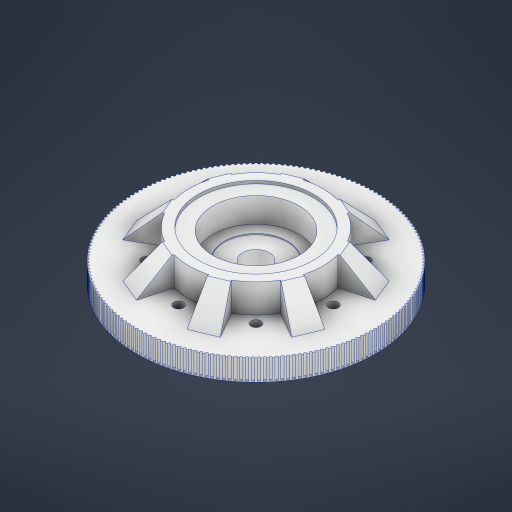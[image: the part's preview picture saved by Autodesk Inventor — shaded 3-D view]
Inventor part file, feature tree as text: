
AUTODESK INVENTOR PART (.ipt)
format: ipt  version: 2024 (Build 280153000, 153)  size: 658,944 bytes
history: native  units: mm
features: extrude x8, sketch x8, pattern_circular x2, chamfer x1, projected_geometry x1
ambient origin geometry x8: Origin, YZ Plane, XZ Plane, XY Plane, X Axis, Y Axis, Z Axis, Center Point
bodies: Solid1 (feature_tree)
feature tree (20):
  extrude  "Extrusion1"  Depth=22.0mm TaperAngle=0.0deg
  extrude  "Extrusion2"  Depth=21.0mm TaperAngle=0.0deg
  extrude  "Extrusion3"  Depth=90.0mm
  pattern_circular  "Circular Pattern1"  Count=14  [1 undecoded]
  extrude  "Extrusion4"  Depth=3.0mm TaperAngle=0.0deg
  extrude  "Extrusion5"  Depth=80.0mm TaperAngle=360.0deg
  extrude  "Extrusion6"  TaperAngle=15.0deg  [1 undecoded]
  extrude  "Extrusion7"  Depth=1.308997mm
  extrude  "Extrusion8"  Depth=30.0mm TaperAngle=0.0deg
  chamfer  "Chamfer1"  Distance=30.0mm Angle=45.0deg
  pattern_circular  "Circular Pattern2"  Count=8 Angle=360.0deg
  sketch  "Sketch1"  dims[d0=250.0mm d1=22.0mm d2=0.0mm]
  sketch  "Sketch2"  dims[d3=30.0mm d4=0.0mm d5=21.0mm d6=0.0mm]
  projected_geometry  "Projected Loop1"
  sketch  "Sketch3"  dims[d7=1800.0mm d8=360.0deg d10=90.0mm d11=140.0mm]
  sketch  "Sketch4"  dims[d12=1.0mm d13=0.0mm d14=3.0mm d15=0.0mm]
  sketch  "Sketch5"  dims[d16=25.0mm d17=0.0mm d18=80.0mm d20=360.0deg]
  sketch  "Sketch6"  dims[d22=20.0mm d23=0.0mm d24=15.0deg]
  sketch  "Sketch7"  dims[d25=60.0deg d26=1.308997mm]
  sketch  "Sketch8"  dims[d27=1.308997mm d28=30.0mm d29=0.0mm d30=30.0mm d31=2.0mm d32=45.0deg d33=80.0mm d34=360.0deg]
note: 2 required parameter values undecoded (feature->parameter linkage not recoverable at this tier; creation-order binding heuristic only, values carry confidence <= 0.55)
